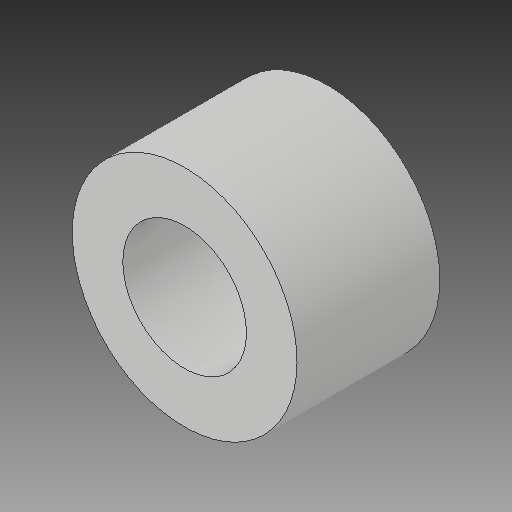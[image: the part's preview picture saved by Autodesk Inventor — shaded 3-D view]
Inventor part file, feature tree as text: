
AUTODESK INVENTOR PART (.ipt)
format: ipt  version: 2018 (Build 220112000, 112)  size: 102,400 bytes
history: native  units: mm
features: other x3, sketch x1
ambient origin geometry x8: Origin, YZ Plane, XZ Plane, XY Plane, X Axis, Y Axis, Z Axis, Center Point
bodies: Solid1 (feature_tree)
feature tree (4):
  other  "Small-Aluminium-Spacer_MIR.ipt"
  other  "Solid1::Small-Aluminium-Spacer_MIR.ipt"
  other  "TaggingFeature1"
  sketch  "Sketch1"  dims[d0=10.0mm]
